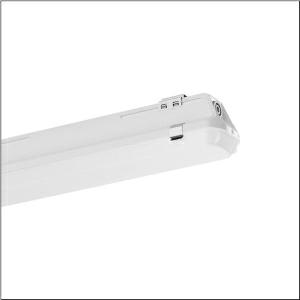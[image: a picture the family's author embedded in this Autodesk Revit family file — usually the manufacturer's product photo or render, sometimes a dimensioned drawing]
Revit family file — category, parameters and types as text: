
# Revit family: monsun_r__11_51fp107p430h_5718
name_source: partatom
category: Lighting Fixtures
units: mm (PartAtom-declared; Revit-internal decimal feet)

## family parameters
Cut with Voids When Loaded = No
Host = Face
Light Source = No
Part Type = Normal
Room Calculation Point = No
Round Connector Dimension = Use Diameter
Shared = No

## types (1)
- Monsun® 11 (1 x LED, 3970 lm, 22.2 W, 4000K)
    Apparent Load = 22 VA
    CIE Flux Codes = 47 77 93 94 100
    Color Rendering = 80
    Color Temperature = 4000K
    Default Elevation = 1800 mm
    Description = Monsun® 11, damp-proof luminaire, chain hanger, primary optical cover: enclosure, of PMMA, light emission: direct distribution, primary light characteristic: symmetric, installation type: suspended mounting, surface-mounted, horizontal mounting, vertical mounting, LED, rated luminous flux: 3.970lm, luminous efficacy: 179lm/W, light colour: 840, colour temperature: 4000K, control gear: ECG, with terminal, 3-pole, max. 2.5mm², mains connection: 220..240V, AC, 50/60Hz, rated input power: 22W, luminaire housing, of glass-fibre reinforced polyester, uncoated, bright grey, incl. chain hanger, length: 1.590mm, width: 90mm, height: 88mm, clip for enclosure, of stainless steel (V2A), ceiling mounting element, of stainless steel (V2A), chain hanger, of stainless steel (V2A), protection rating (complete): IP66, insulation class (complete): insulation class I (protective earthing), certification: CE, ENEC, VDE, UKCA, protection symbol: D, impact resistance: IK04, permissible operating ambient temperature: -35..+40°C, standard: EN 50419, EN 60598-2-1, no direct snow, no direct sun, no direct rain, for indoor or canopied outdoor use, corresponds to IFS (International Featured Standards) requirements for safety and quality in the food industry, contact your sales advisor before using the luminaires in applications with unclear chemical exposure, large temperature fluctuations or condensation-forming humidity, LABS conformity tested according to VDMA 24364:2018-05, packaging unit: 1 piece
    Height = 89 mm
    Lamp = 1 x LED
    Lamp Light Flux = 3970 lm
    Lamp Power = 22.2 W
    Lamp count = 1
    Length = 1590 mm
    Luminous efficacy = 179 lm/W
    Manufacturer = Siteco
    ModVariant = No
    Model = 51FP107P430H
    Mounting Place = Ceiling
    Mounting Type = Surface mounted
    Number of Poles = 1
    OnlyDefault = Yes
    Power Factor = 1
    Product Name = Monsun® 11
    Product group = damp-proof luminaire
    ProductGroupID = 301
    Protection Class = Protection class I
    Protection Degree = IP 66
    RLX_Detail_Level = 1
    RLX_Emergency_Light_Flux = 0 lm
    RLX_Emergency_Type = 0
    RLX_Emergency_Type_DB = No
    RlxData = <blob elided: 88537 chars, md5=7f2cbbcf>
    Socket = socket
    Standby Power = 0 W
    System Light Flux = 3970 lm
    System Power = 22 W
    Type Comments = Product without accessories
    Type Image = l_1004748.jpg
    URL = http://relux.com
    VarID = ---
    Voltage = 0 V
    Weight = 0.00 kg
    Width = 90 mm

## geometry (parser evidence)
native form markers: Blend x4, Sweep x14
no freeform markers — native parametric forms only
